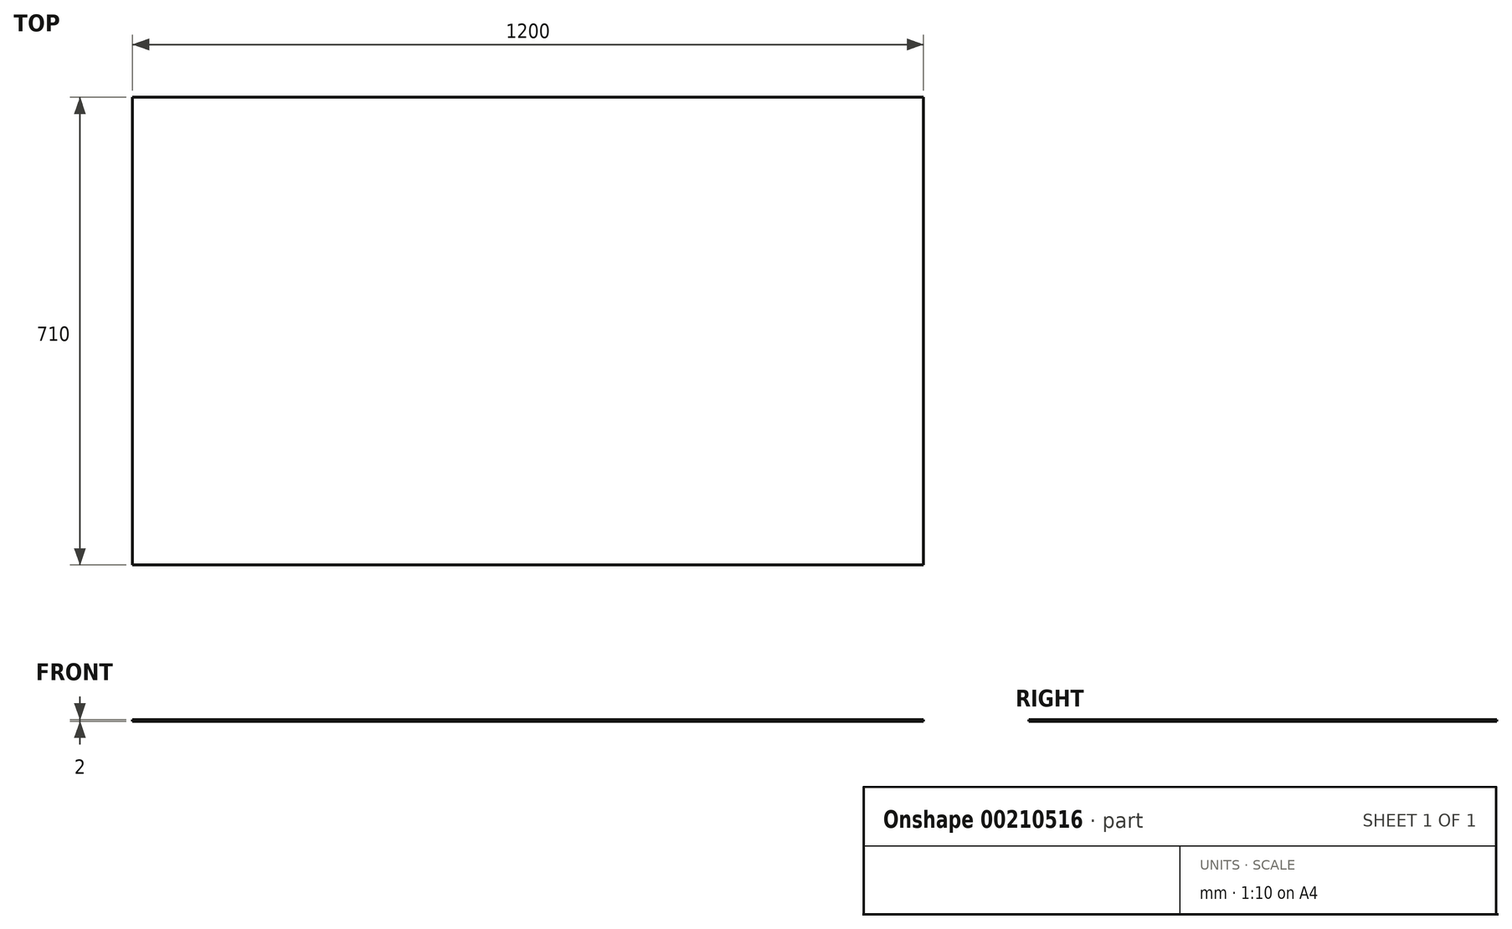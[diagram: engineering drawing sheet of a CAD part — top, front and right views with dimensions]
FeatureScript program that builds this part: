
annotation { "Feature Type Name" : "Feature", "Feature Type Description" : "" }
export const myFeature = defineFeature(function(context is Context, id is Id, definition is map)
    precondition{}
    {
        {
            var Q0;
            Q0=qCreatedBy(makeId("Top.planeOp"),FACE);
            var sketch = newSketch(context, id + "F0", { "sketchPlane" : qUnion([Q0])});
            skLineSegment(sketch, "E0.bottom", {"start": v(-593.19, 404.6) * mm, "end": v(606.81, 404.6) * mm});
            skLineSegment(sketch, "E0.top", {"start": v(-593.19, -305.4) * mm, "end": v(606.81, -305.4) * mm});
            skLineSegment(sketch, "E0.left", {"start": v(-593.19, 404.6) * mm, "end": v(-593.19, -305.4) * mm});
            skLineSegment(sketch, "E0.right", {"start": v(606.81, 404.6) * mm, "end": v(606.81, -305.4) * mm});
            skSolve(sketch);
        }
        {
            var Q0;
            Q0=makeQuery(id+"F0.imprint","IMPRINT",FACE,{"disambiguationData":[TD([[makeQuery(id+"F0.imprint","IMPRINT",EDGE,{"derivedFrom":sQuery(id+"F0.wireOp",EDGE,"E0.bottom")}),-1.0]])]});
            extrude(context, id + "F1", {"entities" : qUnion([Q0]), "depth" : 2 * mm});
        }
    });
